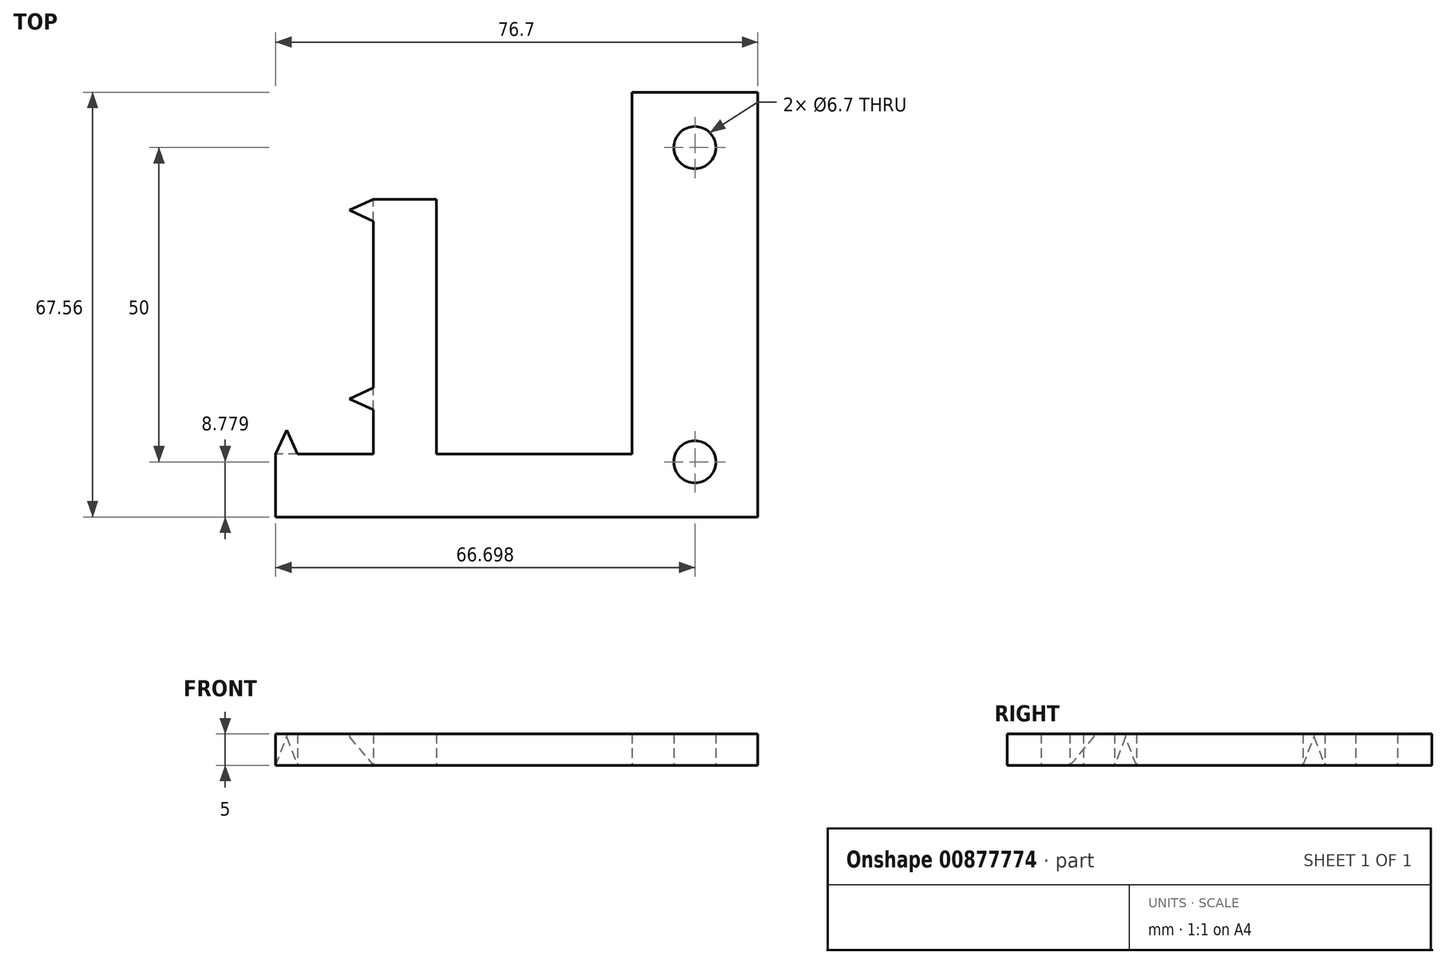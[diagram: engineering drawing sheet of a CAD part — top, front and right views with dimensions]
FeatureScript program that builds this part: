
annotation { "Feature Type Name" : "Feature", "Feature Type Description" : "" }
export const myFeature = defineFeature(function(context is Context, id is Id, definition is map)
    precondition{}
    {
        {
            var Q0;
            Q0=qCreatedBy(makeId("Top.planeOp"),FACE);
            var sketch = newSketch(context, id + "F0", { "sketchPlane" : qUnion([Q0])});
            skLineSegment(sketch, "E0.top", {"start": v(15.56, 50.56) * mm, "end": v(25.56, 50.56) * mm});
            skLineSegment(sketch, "E0.left", {"start": v(15.56, 10) * mm, "end": v(15.56, 50.56) * mm});
            skLineSegment(sketch, "E0.right", {"start": v(25.56, 10) * mm, "end": v(25.56, 50.56) * mm});
            skLineSegment(sketch, "E1.top", {"start": v(76.7, 0) * mm, "end": v(0, 0) * mm});
            skLineSegment(sketch, "E1.right", {"start": v(0, 10) * mm, "end": v(0, 0) * mm});
            skLineSegment(sketch, "E2", {"start": v(0, 10) * mm, "end": v(15.56, 10) * mm});
            skPoint(sketch, "E3.0.midPoint", {"position": v(0, 10) * mm});
            skPoint(sketch, "E4.0.midPoint", {"position": v(15.56, 50.56) * mm});
            skLineSegment(sketch, "E5", {"start": v(0, 10) * mm, "end": v(1.75, 13.8) * mm});
            skLineSegment(sketch, "E6", {"start": v(1.75, 13.81) * mm, "end": v(1.75, 10) * mm, "construction": true});
            skLineSegment(sketch, "E7", {"start": v(1.75, 13.8) * mm, "end": v(3.5, 10) * mm});
            skLineSegment(sketch, "E8", {"start": v(15.56, 50.56) * mm, "end": v(11.75, 48.8) * mm});
            skLineSegment(sketch, "E9", {"start": v(11.75, 48.8) * mm, "end": v(15.56, 47.06) * mm});
            skLineSegment(sketch, "E10", {"start": v(11.75, 48.8) * mm, "end": v(15.56, 48.8) * mm, "construction": true});
            skLineSegment(sketch, "E11", {"start": v(15.56, 17.06) * mm, "end": v(11.75, 18.8) * mm});
            skLineSegment(sketch, "E12", {"start": v(11.75, 18.8) * mm, "end": v(15.56, 18.8) * mm});
            skLineSegment(sketch, "E13", {"start": v(15.56, 18.81) * mm, "end": v(11.75, 18.81) * mm, "construction": true});
            skLineSegment(sketch, "E14", {"start": v(11.75, 18.8) * mm, "end": v(15.56, 20.56) * mm});
            skLineSegment(sketch, "E15.bottom", {"start": v(25.56, 10) * mm, "end": v(56.7, 10) * mm});
            skLineSegment(sketch, "E16.top", {"start": v(56.7, 67.56) * mm, "end": v(76.7, 67.56) * mm});
            skLineSegment(sketch, "E16.left", {"start": v(56.7, 10) * mm, "end": v(56.7, 67.56) * mm});
            skLineSegment(sketch, "E16.right", {"start": v(76.7, 0) * mm, "end": v(76.7, 67.56) * mm});
            skCircle(sketch, "E17", {"center": v(66.7, 8.78) * mm, "radius": 3.35 * mm});
            skCircle(sketch, "E18", {"center": v(66.7, 58.78) * mm, "radius": 3.35 * mm});
            skLineSegment(sketch, "E19", {"start": v(66.7, 8.78) * mm, "end": v(66.7, 58.78) * mm, "construction": true});
            skLineSegment(sketch, "E20", {"start": v(66.7, 58.78) * mm, "end": v(66.7, 67.56) * mm, "construction": true});
            skLineSegment(sketch, "E21", {"start": v(66.7, 8.78) * mm, "end": v(66.7, 0) * mm, "construction": true});
            skSolve(sketch);
        }
        {
            var Q0;
            {var subQ0=sQuery(id+"F0.wireOp",EDGE,"E6");Q0=makeQuery(id+"F0.imprint","IMPRINT",FACE,{"disambiguationData":[TD([[makeQuery(id+"F0.imprint","IMPRINT",EDGE,{"derivedFrom":subQ0}),1.0]])]});}
            var Q1;
            {var subQ0=sQuery(id+"F0.wireOp",EDGE,"E5");Q1=makeQuery(id+"F0.imprint","IMPRINT",FACE,{"disambiguationData":[TD([[makeQuery(id+"F0.imprint","IMPRINT",EDGE,{"derivedFrom":subQ0}),-1.0]])]});}
            var Q2;
            {var subQ0=sQuery(id+"F0.wireOp",EDGE,"E13");Q2=makeQuery(id+"F0.imprint","IMPRINT",FACE,{"disambiguationData":[TD([[makeQuery(id+"F0.imprint","IMPRINT",EDGE,{"derivedFrom":subQ0}),-1.0]])]});}
            var Q3;
            {var subQ0=sQuery(id+"F0.wireOp",EDGE,"E9");Q3=makeQuery(id+"F0.imprint","IMPRINT",FACE,{"disambiguationData":[TD([[makeQuery(id+"F0.imprint","IMPRINT",EDGE,{"derivedFrom":subQ0}),1.0]])]});}
            var Q4;
            {var subQ0=sQuery(id+"F0.wireOp",EDGE,"E8");Q4=makeQuery(id+"F0.imprint","IMPRINT",FACE,{"disambiguationData":[TD([[makeQuery(id+"F0.imprint","IMPRINT",EDGE,{"derivedFrom":subQ0}),1.0]])]});}
            var Q5;
            {var subQ1=sQuery(id+"F0.wireOp",EDGE,"E0.top");Q5=makeQuery(id+"F0.imprint","IMPRINT",FACE,{"disambiguationData":[TD([[makeQuery(id+"F0.imprint","IMPRINT",EDGE,{"derivedFrom":subQ1}),-1.0]])]});}
            var Q6;
            {var subQ0=sQuery(id+"F0.wireOp",EDGE,"E0.bottom");Q6=makeQuery(id+"F0.imprint","IMPRINT",FACE,{"disambiguationData":[TD([[makeQuery(id+"F0.imprint","IMPRINT",EDGE,{"derivedFrom":subQ0}),1.0]])]});}
            var Q7;
            {var subQ0=sQuery(id+"F0.wireOp",EDGE,"E15.bottom");Q7=makeQuery(id+"F0.imprint","IMPRINT",FACE,{"disambiguationData":[TD([[makeQuery(id+"F0.imprint","IMPRINT",EDGE,{"derivedFrom":subQ0}),-1.0]])]});}
            var Q8;
            {var subQ3=sQuery(id+"F0.wireOp",EDGE,"mJTOkjZh-mPq2-TIPx-lQhC-wYbBk8UAqeif");Q8=makeQuery(id+"F0.imprint","IMPRINT",FACE,{"disambiguationData":[TD([[makeQuery(id+"F0.imprint","IMPRINT",EDGE,{"derivedFrom":subQ3}),-1.0]])]});}
            var Q9;
            {var subQ0=sQuery(id+"F0.wireOp",EDGE,"E16.left");var subQ5=sQuery(id+"F0.wireOp",EDGE,"E16.top");var subQ9=makeQuery(id+"F0.imprint","INTERSECT",VERTEX,{"derivedFrom":[subQ5,subQ0]});Q9=makeQuery(id+"F0.imprint","IMPRINT",FACE,{"disambiguationData":[TD([[makeQuery(id+"F0.imprint","IMPRINT",EDGE,{"disambiguationData":[TD([[subQ9,-1.0]])],"derivedFrom":subQ5}),-1.0]])]});}
            var Q10;
            {var subQ5=sQuery(id+"F0.wireOp",EDGE,"E16.right");Q10=makeQuery(id+"F0.imprint","IMPRINT",FACE,{"disambiguationData":[TD([[makeQuery(id+"F0.imprint","IMPRINT",EDGE,{"derivedFrom":subQ5}),1.0]])]});}
            var Q11;
            {var subQ1=sQuery(id+"F0.wireOp",EDGE,"E1.right");Q11=makeQuery(id+"F0.imprint","IMPRINT",FACE,{"disambiguationData":[TD([[makeQuery(id+"F0.imprint","IMPRINT",EDGE,{"derivedFrom":subQ1}),1.0]])]});}
            var Q12;
            {var subQ0=sQuery(id+"F0.wireOp",EDGE,"E12");Q12=makeQuery(id+"F0.imprint","IMPRINT",FACE,{"disambiguationData":[TD([[makeQuery(id+"F0.imprint","IMPRINT",EDGE,{"derivedFrom":subQ0}),1.0]])]});}
            var Q13;
            {var subQ0=sQuery(id+"F0.wireOp",EDGE,"E11");Q13=makeQuery(id+"F0.imprint","IMPRINT",FACE,{"disambiguationData":[TD([[makeQuery(id+"F0.imprint","IMPRINT",EDGE,{"derivedFrom":subQ0}),-1.0]])]});}
            extrude(context, id + "F1", {"entities" : qUnion([Q0, Q1, Q2, Q3, Q4, Q5, Q6, Q7, Q8, Q9, Q10, Q11, Q12, Q13]), "depth" : 5 * mm, "offsetDistance" : 25 * mm});
        }
        {
            var Q0;
            Q0=makeQuery(id+"F1.opExtrude","SWEPT_FACE",FACE,{"disambiguationData":[OSD([sQuery(id+"F0.wireOp",EDGE,"E0.top")])]});
            var sketch = newSketch(context, id + "F2", { "sketchPlane" : qUnion([Q0])});
            skLineSegment(sketch, "E22", {"start": v(-15.56, 0) * mm, "end": v(-11.75, 4.5) * mm});
            skLineSegment(sketch, "E23", {"start": v(-11.75, 4.5) * mm, "end": v(-11.75, 0) * mm});
            skLineSegment(sketch, "E24", {"start": v(-11.75, 0) * mm, "end": v(-15.56, 0) * mm});
            skSolve(sketch);
        }
        {
            var Q0;
            Q0 = qSketchRegion(id + "F2", true);
            var Q1;
            Q1=makeQuery(id+"F1.opExtrude","SWEPT_FACE",FACE,{"disambiguationData":[OSD([sQuery(id+"F0.wireOp",EDGE,"E2")])]});
            extrude(context, id + "F3", {"entities" : qUnion([Q0]), "operationType" : NewBodyOperationType.REMOVE, "endBound" : BoundingType.UP_TO_SURFACE, "oppositeDirection" : true, "depth" : 25 * mm, "endBoundEntityFace" : qUnion([Q1]), "offsetDistance" : 25 * mm});
        }
        {
            var Q0;
            Q0=makeQuery(id+"F1.opExtrude","SWEPT_FACE",FACE,{"disambiguationData":[OSD([sQuery(id+"F0.wireOp",EDGE,"E1.right")])]});
            var sketch = newSketch(context, id + "F4", { "sketchPlane" : qUnion([Q0])});
            skLineSegment(sketch, "E25", {"start": v(-10, 0) * mm, "end": v(-13.8, 4.5) * mm});
            skLineSegment(sketch, "E26", {"start": v(-13.8, 4.5) * mm, "end": v(-13.8, 0) * mm});
            skLineSegment(sketch, "E27", {"start": v(-13.8, 0) * mm, "end": v(-10, 0) * mm});
            skSolve(sketch);
        }
        {
            var Q0;
            Q0 = qSketchRegion(id + "F4", true);
            var Q1;
            {var subQ0=sQuery(id+"F0.wireOp",EDGE,"E0.left");Q1=makeQuery(id+"F1.opExtrude","SWEPT_FACE",FACE,{"disambiguationData":[OSD([subQ0]),TDD([makeQuery(id+"F0.imprint","IMPRINT",EDGE,{"disambiguationData":[TD([[makeQuery(id+"F0.imprint","INTERSECT",VERTEX,{"derivedFrom":[subQ0,sQuery(id+"F0.wireOp",EDGE,"E11")]}),1.0]])],"derivedFrom":subQ0})])]});}
            extrude(context, id + "F5", {"entities" : qUnion([Q0]), "operationType" : NewBodyOperationType.REMOVE, "endBound" : BoundingType.UP_TO_SURFACE, "oppositeDirection" : true, "depth" : 25 * mm, "endBoundEntityFace" : qUnion([Q1]), "offsetDistance" : 25 * mm});
        }
    });
